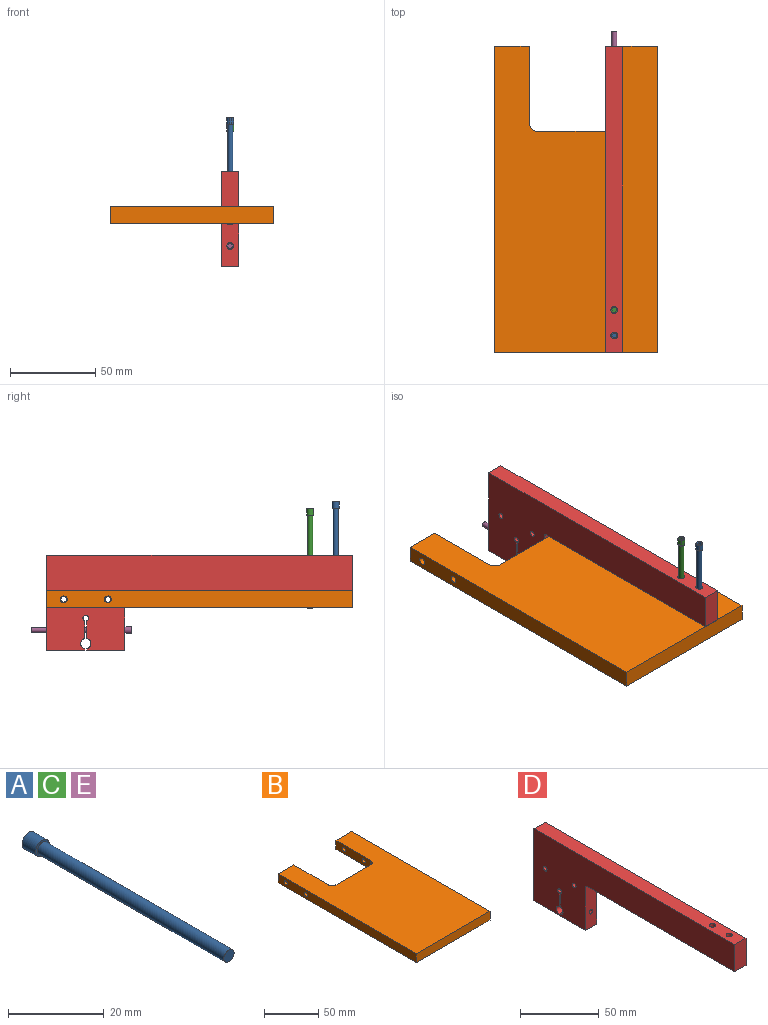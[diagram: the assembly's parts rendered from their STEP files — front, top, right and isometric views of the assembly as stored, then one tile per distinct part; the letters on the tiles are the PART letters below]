
ASSEMBLY  parts=5 mates=7
PART A: 12 faces, bbox 4x59x4 mm
  f0: plane 4x1.25mm, normal (0.87,0,0.5), area 5.8mm2, adj f1,f6,f7,f11
  f1: plane 4x1.44mm, normal (0,0,1), area 5.8mm2, adj f0,f2,f7,f11
  f2: plane 4x1.25mm, normal (-0.87,0,0.5), area 5.8mm2, adj f1,f3,f7,f11
  f3: plane 4x1.25mm, normal (-0.87,0,-0.5), area 5.8mm2, adj f2,f4,f7,f11
  f4: plane 4x1.44mm, normal (0,0,-1), area 5.8mm2, adj f3,f6,f7,f11
  f5: cylinder r=2mm len=4mm, axis (0,-1,0), area 50.3mm2, adj f7,f8
  f6: plane 4x1.25mm, normal (0.87,0,-0.5), area 5.8mm2, adj f0,f4,f7,f11
  f7: plane 4x4mm, normal (0,1,0), area 7.2mm2, adj f0,f1,f2,f3,f4,f5,f6
  f8: plane 4x4mm, normal (0,-1,0), area 5.5mm2, adj f5,f10
  f9: plane 3x3mm, normal (0,-1,0), area 7.1mm2, adj f10
  f10: cylinder r=1.5mm len=55mm, axis (0,1,0), area 518.4mm2, adj f8,f9
  f11: plane 2.89x2.5mm, normal (0,1,0), area 5.4mm2, adj f0,f1,f2,f3,f4,f6
PART B: 16 faces, bbox 96x180x10 mm
  f0: plane 96x10mm, normal (0,-1,0), area 960mm2, adj f1,f6,f7,f10
  f1: plane 180x10mm, normal (1,0,0), area 1774.9mm2, adj f0,f2,f6,f7,f8,f9
  f2: plane 20.5x10mm, normal (0,1,0), area 205mm2, adj f1,f3,f6,f7
  f3: plane 45x10mm, normal (-1,0,0), area 424.9mm2, adj f2,f4,f6,f7,f8,f9
  f4: cylinder r=5mm len=10mm, axis (0,0,-1), area 78.5mm2, adj f3,f5,f6,f7
  f5: plane 45x10mm, normal (0,1,0), area 450mm2, adj f4,f6,f7,f13
  f6: plane 180x96mm, normal (0,0,1), area 14540.7mm2, adj f0,f1,f2,f3,f4,f5,f10,f11
  f7: plane 180x96mm, normal (0,0,-1), area 14540.7mm2, adj f0,f1,f2,f3,f4,f5,f10,f11
  f8: cylinder r=2mm len=20.5mm, axis (1,0,0), area 257.6mm2, adj f1,f3
  f9: cylinder r=2mm len=20.5mm, axis (1,0,0), area 257.6mm2, adj f1,f3
  f10: plane 180x10mm, normal (-1,0,0), area 1774.9mm2, adj f0,f6,f7,f11,f14,f15
  f11: plane 20.5x10mm, normal (0,1,0), area 205mm2, adj f6,f7,f10,f12
  f12: plane 45x10mm, normal (1,0,0), area 424.9mm2, adj f6,f7,f11,f13,f14,f15
  f13: cylinder r=5mm len=10mm, axis (0,0,-1), area 78.5mm2, adj f5,f6,f7,f12
  f14: cylinder r=2mm len=20.5mm, axis (-1,0,0), area 257.6mm2, adj f10,f12
  f15: cylinder r=2mm len=20.5mm, axis (-1,0,0), area 257.6mm2, adj f10,f12
PART C: same geometry as A
PART D: 25 faces, bbox 10x179.9x56 mm
  f0: plane 22.5x10mm, normal (0,0,-1), area 225mm2, adj f1,f16,f17,f18
  f1: plane 10x1.04mm, normal (0,-1,0), area 10.4mm2, adj f0,f2,f17,f18
  f2: cylinder r=3mm len=10mm, axis (1,0,0), area 84.2mm2, adj f1,f3,f17,f18
  f3: plane 10.47x10mm, normal (0,-1,0), area 97.6mm2, adj f2,f4,f17,f18,f19
  f4: cylinder r=1.65mm len=10mm, axis (1,0,0), area 93.5mm2, adj f3,f5,f17,f18
  f5: plane 10.47x10mm, normal (0,1,0), area 97.6mm2, adj f4,f6,f17,f18,f20
  f6: cylinder r=3mm len=10mm, axis (1,0,0), area 84.2mm2, adj f5,f7,f17,f18
  f7: plane 10x1.04mm, normal (0,1,0), area 10.4mm2, adj f6,f8,f17,f18
  f8: plane 22.5x10mm, normal (0,0,-1), area 225mm2, adj f7,f9,f17,f18
  f9: plane 33.35x10mm, normal (0,-1,0), area 326.4mm2, adj f8,f10,f17,f18,f20
  f10: cylinder r=1.65mm len=10mm, axis (1,0,0), area 25.9mm2, adj f9,f11,f17,f18
  f11: plane 132.23x10mm, normal (0,0,-1), area 1322.2mm2, adj f10,f12,f17,f18
  f12: plane 21x10mm, normal (0,-1,0), area 210mm2, adj f11,f13,f17,f18
  f13: plane 179.88x10mm, normal (0,0,1), area 1773.6mm2, adj f12,f16,f17,f18,f21,f23
  f14: cylinder r=1.65mm len=10mm, axis (1,0,0), area 103.7mm2, adj f17,f18
  f15: cylinder r=1.65mm len=10mm, axis (1,0,0), area 103.7mm2, adj f17,f18
  f16: plane 56x10mm, normal (0,1,0), area 552.9mm2, adj f0,f13,f17,f18,f19
  f17: plane 179.88x56mm, normal (-1,0,0), area 5322.6mm2, adj f0,f1,f2,f3,f4,f5,f6,f7
  f18: plane 179.88x56mm, normal (1,0,0), area 5322.6mm2, adj f0,f1,f2,f3,f4,f5,f6,f7
  f19: cylinder r=1.5mm len=22.5mm, axis (0,1,0), area 212.1mm2, adj f3,f16
  f20: cylinder r=1.5mm len=22.5mm, axis (0,1,0), area 212.1mm2, adj f5,f9
  f21: cylinder r=2mm len=20mm, axis (0,0,1), area 251.3mm2, adj f13,f22
  f22: plane 4x4mm, normal (0,0,1), area 12.6mm2, adj f21
  f23: cylinder r=2mm len=20mm, axis (0,0,1), area 251.3mm2, adj f13,f24
  f24: plane 4x4mm, normal (0,0,1), area 12.6mm2, adj f23
PART E: same geometry as A
PLACE A rot(axis=(1,0,0),90deg) t=(-15.75,-137.78,-12.8)mm
PLACE B t=(-15.75,0.22,-16.42)mm
PLACE C rot(axis=(1,0,0),90deg) t=(-15.75,-122.78,-16.78)mm
PLACE D t=(-15.75,0.22,-16.42)mm
PLACE E rot(axis=(1,0,0),180deg) t=(-15.75,53.97,-52.42)mm
MATE planar D.f11 <-> B.f6  axis (0,0,-1) through (6.75,-63.67,-11.42)mm
MATE planar E.f5 <-> D.f9  axis (0,1,0) through (6.75,4.09,-34.42)mm
MATE planar B.f3 <-> D.f4  axis (-1,0,0) through (11.75,50.22,-16.42)mm
MATE cylindrical B.f15 <-> D.f15  axis (1,0,0) through (32.25,14.09,-16.42)mm
MATE cylindrical A.f10 <-> D.f23  axis (0,0,1) through (6.75,-119.78,9.58)mm
MATE cylindrical C.f10 <-> D.f21  axis (0,0,1) through (6.75,-104.78,5.59)mm
MATE cylindrical E.f10 <-> D.f19  axis (0,-1,0) through (6.75,31.59,-34.42)mm
